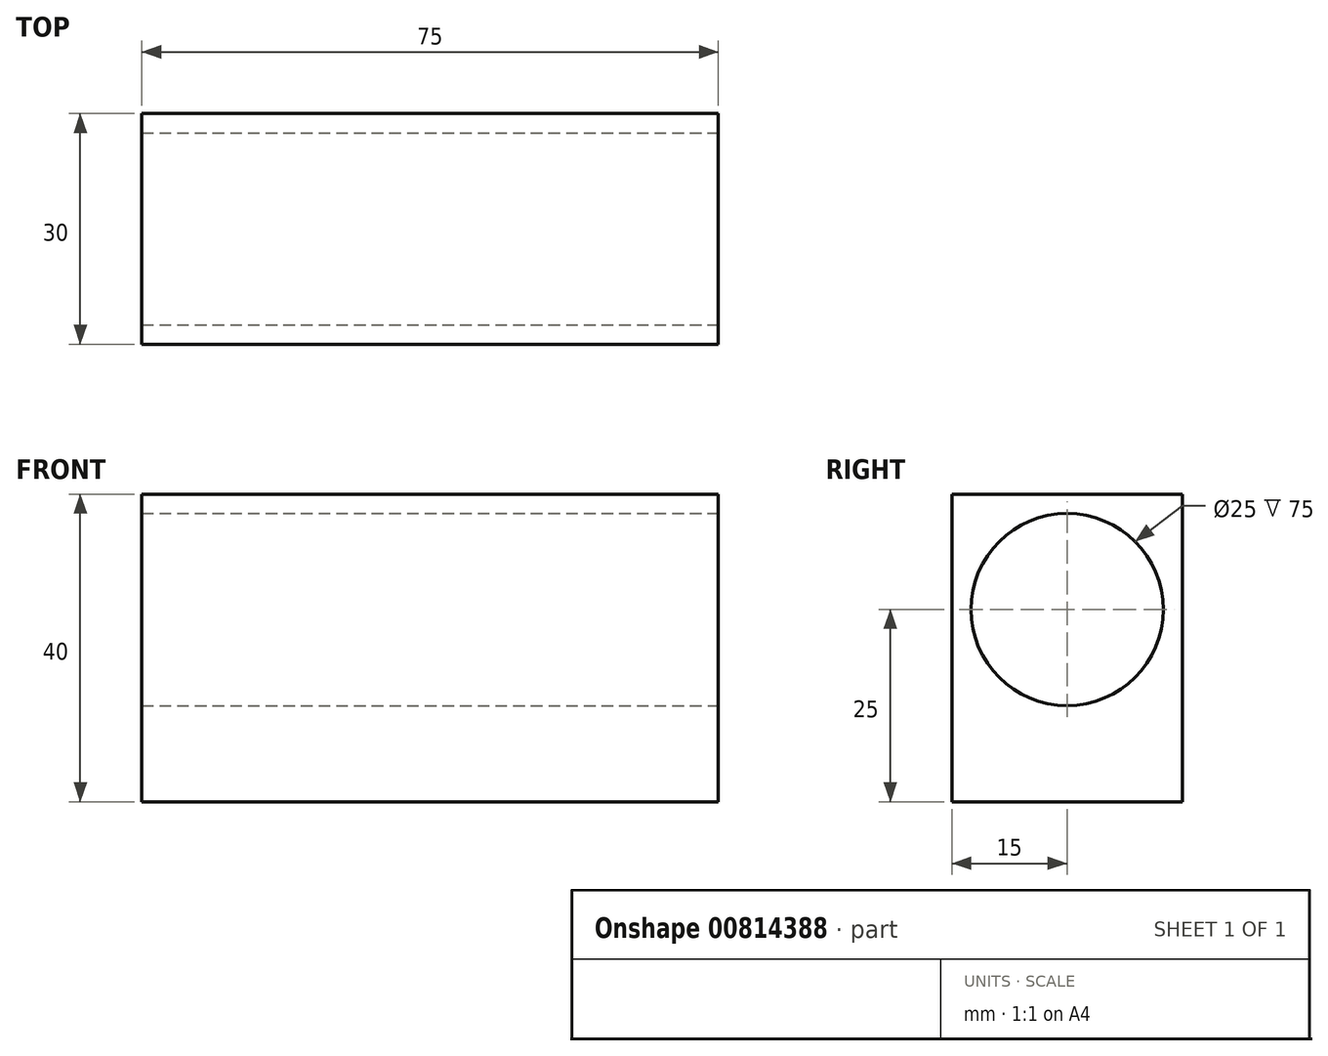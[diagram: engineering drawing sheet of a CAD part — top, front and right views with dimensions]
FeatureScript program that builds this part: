
annotation { "Feature Type Name" : "Feature", "Feature Type Description" : "" }
export const myFeature = defineFeature(function(context is Context, id is Id, definition is map)
    precondition{}
    {
        {
            var Q0;
            Q0=qCreatedBy(makeId("Top.planeOp"),FACE);
            var sketch = newSketch(context, id + "F0", { "sketchPlane" : qUnion([Q0])});
            skLineSegment(sketch, "E0.bottom", {"start": v(37.5, 15) * mm, "end": v(-37.5, 15) * mm});
            skLineSegment(sketch, "E0.top", {"start": v(37.5, -15) * mm, "end": v(-37.5, -15) * mm});
            skLineSegment(sketch, "E0.left", {"start": v(37.5, 15) * mm, "end": v(37.5, -15) * mm});
            skLineSegment(sketch, "E0.right", {"start": v(-37.5, 15) * mm, "end": v(-37.5, -15) * mm});
            skPoint(sketch, "E0.middle", {"position": v(0, 0) * mm});
            skSolve(sketch);
        }
        {
            var Q0;
            Q0=makeQuery(id+"F0.imprint","IMPRINT",FACE,{"disambiguationData":[TD([[makeQuery(id+"F0.imprint","IMPRINT",EDGE,{"derivedFrom":sQuery(id+"F0.wireOp",EDGE,"E0.bottom")}),1.0]])]});
            extrude(context, id + "F1", {"entities" : qUnion([Q0]), "depth" : 40 * mm, "offsetDistance" : 25 * mm});
        }
        {
            var Q0;
            Q0=makeQuery(id+"F1.opExtrude","SWEPT_FACE",FACE,{"disambiguationData":[OSD([sQuery(id+"F0.wireOp",EDGE,"E0.left")])]});
            var sketch = newSketch(context, id + "F2", { "sketchPlane" : qUnion([Q0])});
            skLineSegment(sketch, "E1", {"start": v(12, 40) * mm, "end": v(12, 0) * mm});
            skLineSegment(sketch, "E2", {"start": v(-12, 40) * mm, "end": v(-12, 0) * mm});
            skLineSegment(sketch, "E3", {"start": v(0, 39.87) * mm, "end": v(0, 0) * mm});
            skPoint(sketch, "E3.endSnap0", {"position": v(0, 0) * mm});
            skPoint(sketch, "E4", {"position": v(0, 25) * mm});
            skSolve(sketch);
        }
        {
            var Q0;
            Q0=sQuery(id+"F2.wireOp",VERTEX,"E4");
            var Q1;
            Q1=makeQuery(id+"F1.opExtrude","SWEPT_BODY",BODY,{"disambiguationData":[OSD([sQuery(id+"F0.wireOp",EDGE,"E0.bottom"),sQuery(id+"F0.wireOp",EDGE,"E0.top"),sQuery(id+"F0.wireOp",EDGE,"E0.left"),sQuery(id+"F0.wireOp",EDGE,"E0.right")])]});
            hole(context, id + "F3", {"style" : HoleStyle.SIMPLE, "endStyle" : HoleEndStyle.THROUGH, "holeDiameter" : 25 * mm, "majorDiameter" : 5 * mm, "isTappedThrough" : true, "tappedDepth" : 12 * mm, "tapClearance" : 3, "locations" : qUnion([Q0]), "scope" : qUnion([Q1])});
        }
    });
